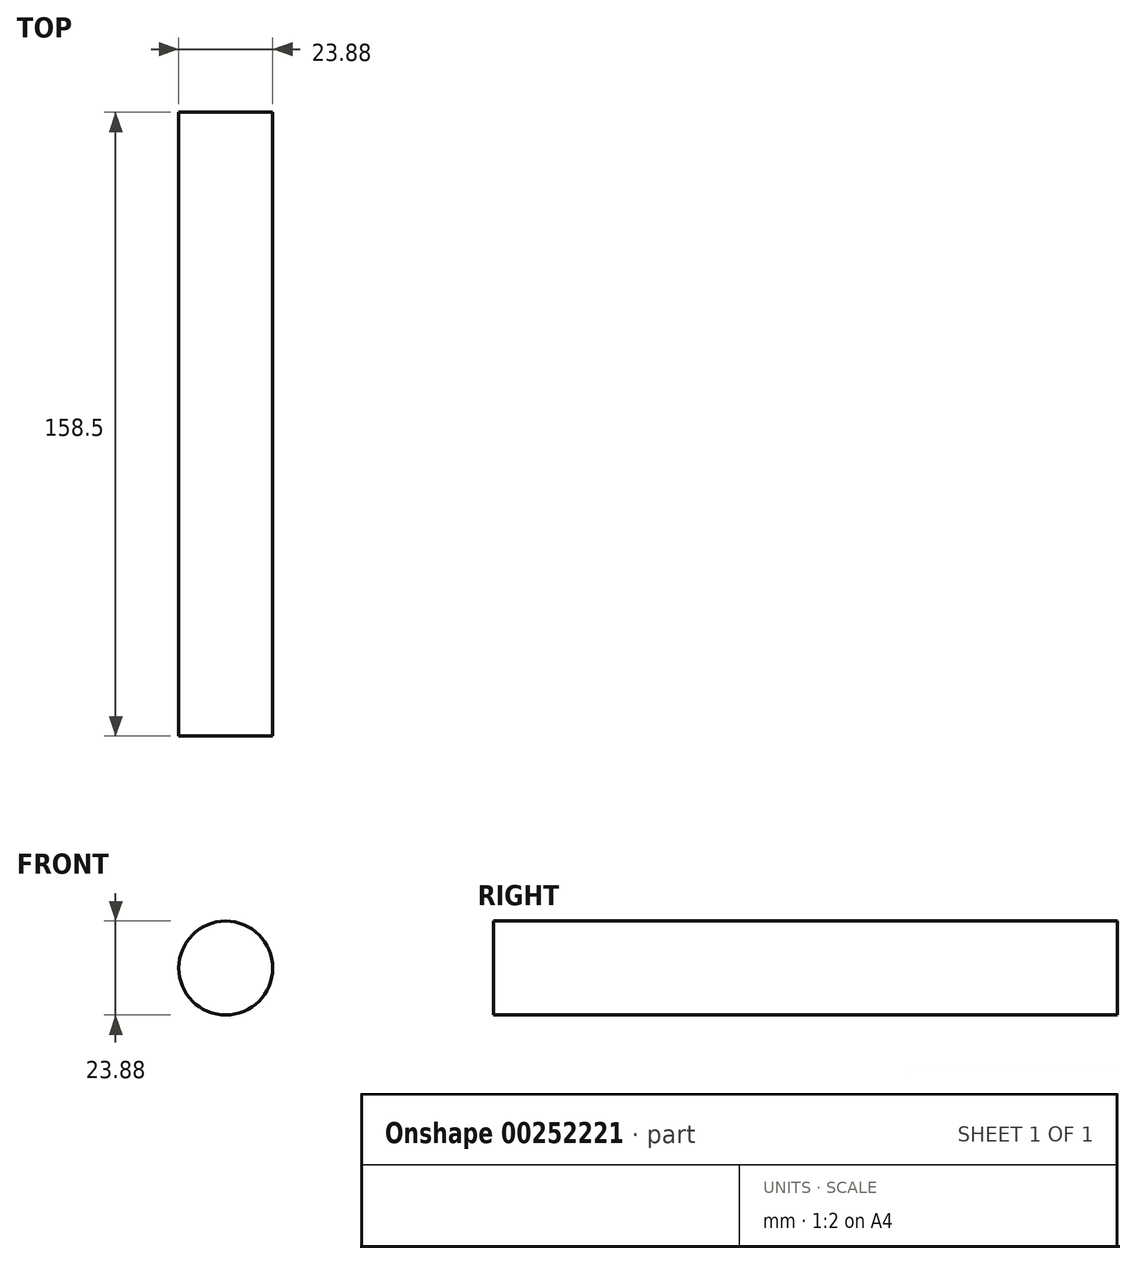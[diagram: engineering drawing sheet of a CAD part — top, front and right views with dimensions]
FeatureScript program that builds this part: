
annotation { "Feature Type Name" : "Feature", "Feature Type Description" : "" }
export const myFeature = defineFeature(function(context is Context, id is Id, definition is map)
    precondition{}
    {
        {
            var Q0;
            Q0=qCreatedBy(makeId("Front.planeOp"),FACE);
            var sketch = newSketch(context, id + "F0", { "sketchPlane" : qUnion([Q0])});
            skCircle(sketch, "E0", {"center": v(0, 0) * mm, "radius": 11.94 * mm});
            skSolve(sketch);
        }
        {
            var Q0;
            Q0 = qSketchRegion(id + "F0", true);
            extrude(context, id + "F1", {"entities" : qUnion([Q0]), "depth" : 158.5 * mm});
        }
    });
